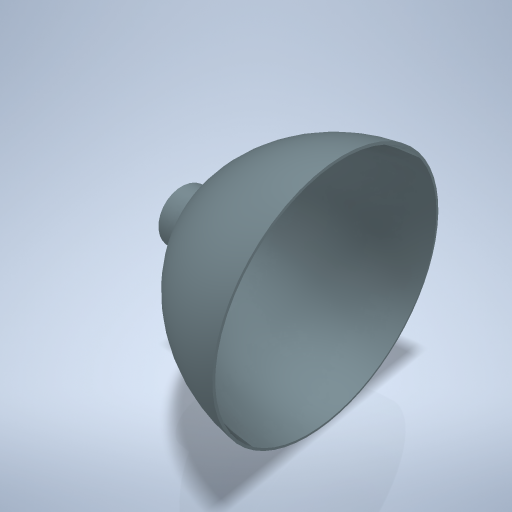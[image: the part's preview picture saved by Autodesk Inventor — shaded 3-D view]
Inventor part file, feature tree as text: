
AUTODESK INVENTOR PART (.ipt)
format: ipt  version: 2024.2 (Build 282272000, 272)  size: 317,440 bytes
history: native  units: mm
features: sketch x4, revolve x2, hole x2, fillet x1, projected_geometry x1
ambient origin geometry x8: Origin, YZ Plane, XZ Plane, XY Plane, X Axis, Y Axis, Z Axis, Center Point
bodies: Volumenkörper1 (feature_tree)
feature tree (10):
  revolve  "Umdrehung1"
  hole  "Bohrung2"  [1 undecoded]
  fillet  "Rundung1"  Radius=6.0mm
  revolve  "Umdrehung2"
  hole  "Bohrung3"  [1 undecoded]
  sketch  "Skizze1"  dims[d0=35.0mm d1=12.0mm d2=6.0mm]
  sketch  "Skizze3"  dims[d5=50.0mm d6=32.0mm]
  sketch  "Skizze5"  dims[d7=90.0deg]
  projected_geometry  "Projizierte Kontur2"
  sketch  "Skizze6"  dims[d17=6.647mm d18=6.0mm d19=4.0mm d20=2.0mm d21=90.0deg d22=6.0mm d23=0.0mm d24=2.0mm d25=1.0mm d26=0.5mm d27=90.0deg d28=50.0mm d29=6.0mm d30=4.0mm d31=2.0mm d32=90.0deg d33=1.0mm d34=0.0mm]
note: 2 required parameter values undecoded (feature->parameter linkage not recoverable at this tier; creation-order binding heuristic only, values carry confidence <= 0.55)
